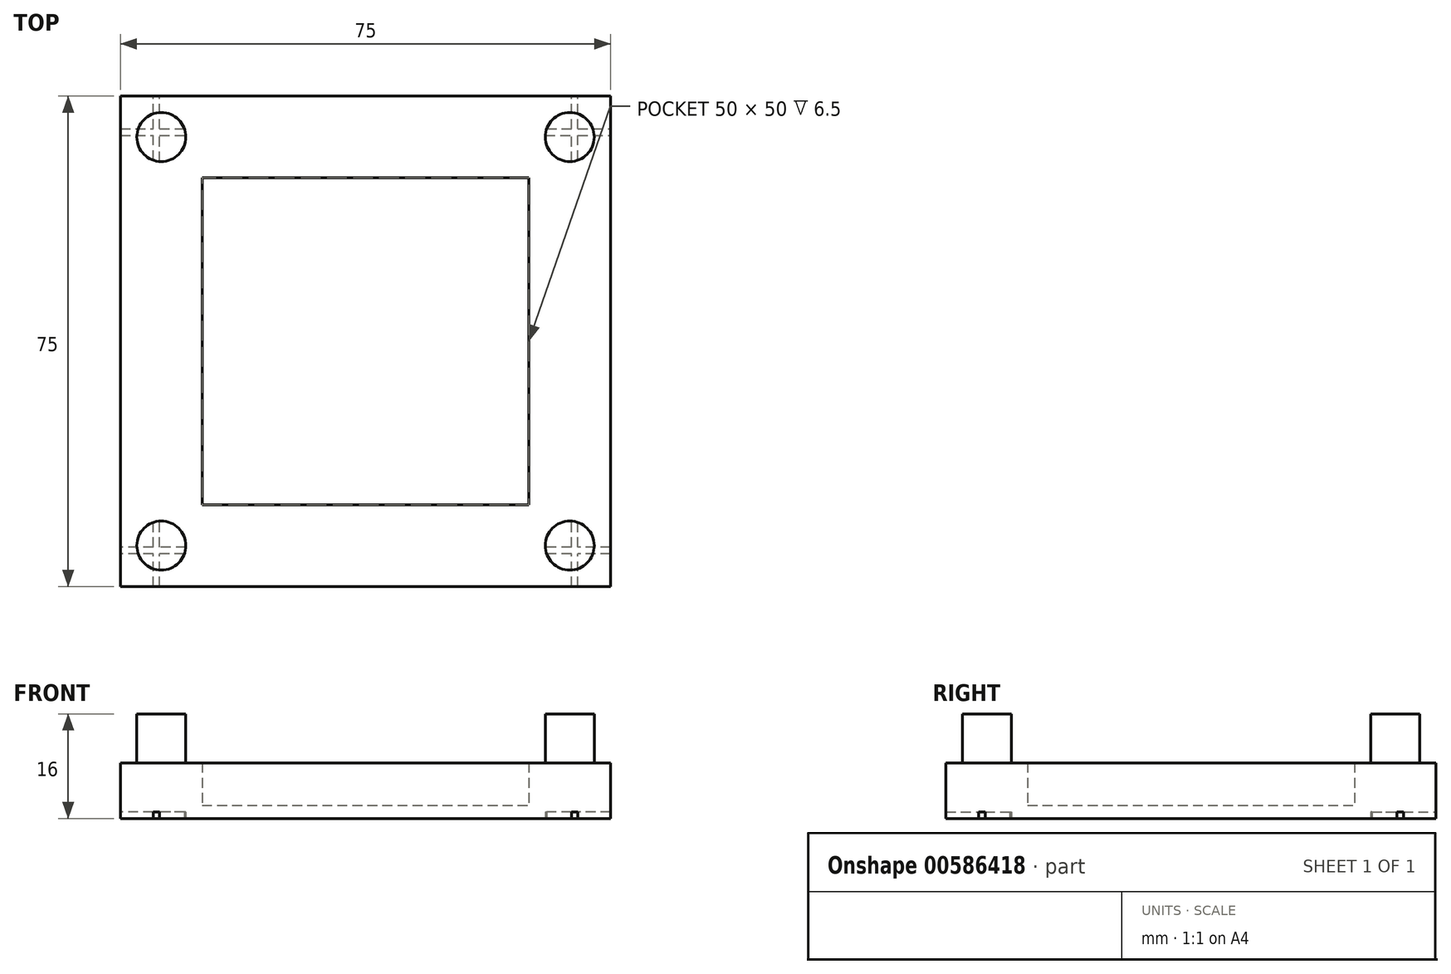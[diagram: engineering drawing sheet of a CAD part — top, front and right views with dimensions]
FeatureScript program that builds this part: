
annotation { "Feature Type Name" : "Feature", "Feature Type Description" : "" }
export const myFeature = defineFeature(function(context is Context, id is Id, definition is map)
    precondition{}
    {
        {
            var Q0;
            Q0=qCreatedBy(makeId("Top.planeOp"),FACE);
            var sketch = newSketch(context, id + "F0", { "sketchPlane" : qUnion([Q0])});
            skLineSegment(sketch, "E0.bottom", {"start": v(-37.5, -37.5) * mm, "end": v(37.5, -37.5) * mm});
            skLineSegment(sketch, "E0.top", {"start": v(-37.5, 37.5) * mm, "end": v(37.5, 37.5) * mm});
            skLineSegment(sketch, "E0.left", {"start": v(-37.5, -37.5) * mm, "end": v(-37.5, 37.5) * mm});
            skLineSegment(sketch, "E0.right", {"start": v(37.5, -37.5) * mm, "end": v(37.5, 37.5) * mm});
            skPoint(sketch, "E0.middle", {"position": v(0, 0) * mm});
            skCircle(sketch, "E1", {"center": v(-31.25, 31.25) * mm, "radius": 3.75 * mm});
            skCircle(sketch, "E2", {"center": v(31.25, 31.25) * mm, "radius": 3.75 * mm});
            skCircle(sketch, "E3", {"center": v(31.25, -31.25) * mm, "radius": 3.75 * mm});
            skCircle(sketch, "E4", {"center": v(-31.25, -31.25) * mm, "radius": 3.75 * mm});
            skSolve(sketch);
        }
        {
            var Q0;
            Q0=makeQuery(id+"F0.imprint","IMPRINT",FACE,{"disambiguationData":[TD([[makeQuery(id+"F0.imprint","IMPRINT",EDGE,{"derivedFrom":sQuery(id+"F0.wireOp",EDGE,"E0.bottom")}),1.0]])]});
            var Q1;
            Q1=makeQuery(id+"F0.imprint","IMPRINT",FACE,{"disambiguationData":[TD([[makeQuery(id+"F0.imprint","IMPRINT",EDGE,{"derivedFrom":sQuery(id+"F0.wireOp",EDGE,"E1")}),1.0]])]});
            var Q2;
            Q2=makeQuery(id+"F0.imprint","IMPRINT",FACE,{"disambiguationData":[TD([[makeQuery(id+"F0.imprint","IMPRINT",EDGE,{"derivedFrom":sQuery(id+"F0.wireOp",EDGE,"E2")}),1.0]])]});
            var Q3;
            Q3=makeQuery(id+"F0.imprint","IMPRINT",FACE,{"disambiguationData":[TD([[makeQuery(id+"F0.imprint","IMPRINT",EDGE,{"derivedFrom":sQuery(id+"F0.wireOp",EDGE,"E3")}),1.0]])]});
            var Q4;
            Q4=makeQuery(id+"F0.imprint","IMPRINT",FACE,{"disambiguationData":[TD([[makeQuery(id+"F0.imprint","IMPRINT",EDGE,{"derivedFrom":sQuery(id+"F0.wireOp",EDGE,"E4")}),1.0]])]});
            extrude(context, id + "F1", {"entities" : qUnion([Q0, Q1, Q2, Q3, Q4]), "depth" : 2 * mm, "offsetDistance" : 25 * mm});
        }
        {
            var Q0;
            Q0=makeQuery(id+"F0.imprint","IMPRINT",FACE,{"disambiguationData":[TD([[makeQuery(id+"F0.imprint","IMPRINT",EDGE,{"derivedFrom":sQuery(id+"F0.wireOp",EDGE,"E4")}),1.0]])]});
            var Q1;
            Q1=makeQuery(id+"F0.imprint","IMPRINT",FACE,{"disambiguationData":[TD([[makeQuery(id+"F0.imprint","IMPRINT",EDGE,{"derivedFrom":sQuery(id+"F0.wireOp",EDGE,"E3")}),1.0]])]});
            var Q2;
            Q2=makeQuery(id+"F0.imprint","IMPRINT",FACE,{"disambiguationData":[TD([[makeQuery(id+"F0.imprint","IMPRINT",EDGE,{"derivedFrom":sQuery(id+"F0.wireOp",EDGE,"E1")}),1.0]])]});
            var Q3;
            Q3=makeQuery(id+"F0.imprint","IMPRINT",FACE,{"disambiguationData":[TD([[makeQuery(id+"F0.imprint","IMPRINT",EDGE,{"derivedFrom":sQuery(id+"F0.wireOp",EDGE,"E2")}),1.0]])]});
            extrude(context, id + "F2", {"entities" : qUnion([Q0, Q1, Q2, Q3]), "operationType" : NewBodyOperationType.ADD, "depth" : 16 * mm, "offsetDistance" : 25 * mm});
        }
        {
            var Q0;
            Q0=makeQuery(id+"F1.opExtrude","CAP_FACE",FACE,{"disambiguationData":[OSD([sQuery(id+"F0.wireOp",EDGE,"E0.bottom"),sQuery(id+"F0.wireOp",EDGE,"E0.top"),sQuery(id+"F0.wireOp",EDGE,"E0.left"),sQuery(id+"F0.wireOp",EDGE,"E0.right")])],"isStart":false});
            var sketch = newSketch(context, id + "F3", { "sketchPlane" : qUnion([Q0])});
            skLineSegment(sketch, "E5.bottom", {"start": v(-25, -25) * mm, "end": v(25, -25) * mm});
            skLineSegment(sketch, "E5.top", {"start": v(-25, 25) * mm, "end": v(25, 25) * mm});
            skLineSegment(sketch, "E5.left", {"start": v(-25, -25) * mm, "end": v(-25, 25) * mm});
            skLineSegment(sketch, "E5.right", {"start": v(25, -25) * mm, "end": v(25, 25) * mm});
            skPoint(sketch, "E5.middle", {"position": v(0, 0) * mm});
            skSolve(sketch);
        }
        {
            var Q0;
            Q0=makeQuery(id+"F3.imprint","IMPRINT",FACE,{"disambiguationData":[TD([[makeQuery(id+"F3.imprint","IMPRINT",EDGE,{"derivedFrom":sQuery(id+"F3.wireOp",EDGE,"E5.bottom")}),-1.0]])]});
            extrude(context, id + "F4", {"entities" : qUnion([Q0]), "operationType" : NewBodyOperationType.ADD, "depth" : 6.5 * mm, "offsetDistance" : 25 * mm});
        }
        {
            var Q0;
            Q0=makeQuery(id+"F0.imprint","IMPRINT",FACE,{"disambiguationData":[TD([[makeQuery(id+"F0.imprint","IMPRINT",EDGE,{"derivedFrom":sQuery(id+"F0.wireOp",EDGE,"E0.bottom")}),1.0]])]});
            var sketch = newSketch(context, id + "F5", { "sketchPlane" : qUnion([Q0])});
            skLineSegment(sketch, "E6.bottom", {"start": v(-32.5, -37.5) * mm, "end": v(-31.5, -37.5) * mm});
            skLineSegment(sketch, "E6.top", {"start": v(-32.5, 37.5) * mm, "end": v(-31.5, 37.5) * mm});
            skLineSegment(sketch, "E6.left", {"start": v(-32.5, -37.5) * mm, "end": v(-32.5, 37.5) * mm});
            skLineSegment(sketch, "E6.right", {"start": v(-31.5, -37.5) * mm, "end": v(-31.5, 37.5) * mm});
            skLineSegment(sketch, "E7.bottom", {"start": v(31.5, -37.5) * mm, "end": v(32.5, -37.5) * mm});
            skLineSegment(sketch, "E7.top", {"start": v(31.5, 37.5) * mm, "end": v(32.5, 37.5) * mm});
            skLineSegment(sketch, "E7.left", {"start": v(31.5, -37.5) * mm, "end": v(31.5, 37.5) * mm});
            skLineSegment(sketch, "E7.right", {"start": v(32.5, -37.5) * mm, "end": v(32.5, 37.5) * mm});
            skLineSegment(sketch, "E8.bottom", {"start": v(37.5, -31.5) * mm, "end": v(-37.5, -31.5) * mm});
            skLineSegment(sketch, "E8.top", {"start": v(37.5, -32.5) * mm, "end": v(-37.5, -32.5) * mm});
            skLineSegment(sketch, "E8.left", {"start": v(37.5, -32.5) * mm, "end": v(37.5, -31.5) * mm});
            skLineSegment(sketch, "E8.right", {"start": v(-37.5, -32.5) * mm, "end": v(-37.5, -31.5) * mm});
            skLineSegment(sketch, "E9.bottom", {"start": v(-37.5, 31.5) * mm, "end": v(37.5, 31.5) * mm});
            skLineSegment(sketch, "E9.top", {"start": v(-37.5, 32.5) * mm, "end": v(37.5, 32.5) * mm});
            skLineSegment(sketch, "E9.left", {"start": v(-37.5, 31.5) * mm, "end": v(-37.5, 32.5) * mm});
            skLineSegment(sketch, "E9.right", {"start": v(37.5, 31.5) * mm, "end": v(37.5, 32.5) * mm});
            skSolve(sketch);
        }
        {
            var Q0;
            {var subQ0=sQuery(id+"F5.wireOp",EDGE,"E7.bottom");Q0=makeQuery(id+"F5.imprint","IMPRINT",FACE,{"disambiguationData":[TD([[makeQuery(id+"F5.imprint","IMPRINT",EDGE,{"derivedFrom":subQ0}),1.0]])]});}
            var Q1;
            {var subQ0=sQuery(id+"F5.wireOp",EDGE,"E8.top");var subQ1=sQuery(id+"F5.wireOp",EDGE,"E7.left");var subQ2=makeQuery(id+"F5.imprint","INTERSECT",VERTEX,{"derivedFrom":[subQ1,subQ0]});Q1=makeQuery(id+"F5.imprint","IMPRINT",FACE,{"disambiguationData":[TD([[makeQuery(id+"F5.imprint","IMPRINT",EDGE,{"disambiguationData":[TD([[subQ2,1.0]])],"derivedFrom":subQ1}),-1.0]])]});}
            var Q2;
            {var subQ0=sQuery(id+"F5.wireOp",EDGE,"E8.top");var subQ1=sQuery(id+"F5.wireOp",EDGE,"E7.right");var subQ2=makeQuery(id+"F5.imprint","INTERSECT",VERTEX,{"derivedFrom":[subQ1,subQ0]});Q2=makeQuery(id+"F5.imprint","IMPRINT",FACE,{"disambiguationData":[TD([[makeQuery(id+"F5.imprint","IMPRINT",EDGE,{"disambiguationData":[TD([[subQ2,-1.0]])],"derivedFrom":subQ1}),-1.0]])]});}
            var Q3;
            {var subQ0=sQuery(id+"F5.wireOp",EDGE,"E8.left");Q3=makeQuery(id+"F5.imprint","IMPRINT",FACE,{"disambiguationData":[TD([[makeQuery(id+"F5.imprint","IMPRINT",EDGE,{"derivedFrom":subQ0}),1.0]])]});}
            var Q4;
            {var subQ0=sQuery(id+"F5.wireOp",EDGE,"E8.top");var subQ1=sQuery(id+"F5.wireOp",EDGE,"E7.left");var subQ2=makeQuery(id+"F5.imprint","INTERSECT",VERTEX,{"derivedFrom":[subQ1,subQ0]});Q4=makeQuery(id+"F5.imprint","IMPRINT",FACE,{"disambiguationData":[TD([[makeQuery(id+"F5.imprint","IMPRINT",EDGE,{"disambiguationData":[TD([[subQ2,-1.0]])],"derivedFrom":subQ1}),-1.0]])]});}
            var Q5;
            {var subQ0=sQuery(id+"F5.wireOp",EDGE,"E8.top");var subQ1=sQuery(id+"F5.wireOp",EDGE,"E7.left");var subQ2=makeQuery(id+"F5.imprint","INTERSECT",VERTEX,{"derivedFrom":[subQ1,subQ0]});Q5=makeQuery(id+"F5.imprint","IMPRINT",FACE,{"disambiguationData":[TD([[makeQuery(id+"F5.imprint","IMPRINT",EDGE,{"disambiguationData":[TD([[subQ2,-1.0]])],"derivedFrom":subQ1}),1.0]])]});}
            var Q6;
            {var subQ0=sQuery(id+"F5.wireOp",EDGE,"E8.bottom");var subQ1=sQuery(id+"F5.wireOp",EDGE,"E7.left");var subQ2=makeQuery(id+"F5.imprint","INTERSECT",VERTEX,{"derivedFrom":[subQ1,subQ0]});Q6=makeQuery(id+"F5.imprint","IMPRINT",FACE,{"disambiguationData":[TD([[makeQuery(id+"F5.imprint","IMPRINT",EDGE,{"disambiguationData":[TD([[subQ2,-1.0]])],"derivedFrom":subQ1}),-1.0]])]});}
            var Q7;
            {var subQ0=sQuery(id+"F5.wireOp",EDGE,"E7.left");var subQ1=makeQuery(id+"F0.imprint","IMPRINT",EDGE,{"derivedFrom":sQuery(id+"F0.wireOp",EDGE,"E3")});var subQ2=makeQuery(id+"F5.imprint","INTERSECT",VERTEX,{"disambiguationData":[OD(1.0)],"derivedFrom":[subQ1,subQ0]});Q7=makeQuery(id+"F5.imprint","IMPRINT",FACE,{"disambiguationData":[TD([[makeQuery(id+"F5.imprint","IMPRINT",EDGE,{"disambiguationData":[TD([[subQ2,-1.0]])],"derivedFrom":subQ0}),-1.0]])]});}
            var Q8;
            {var subQ0=sQuery(id+"F5.wireOp",EDGE,"E8.bottom");var subQ1=makeQuery(id+"F0.imprint","IMPRINT",EDGE,{"derivedFrom":sQuery(id+"F0.wireOp",EDGE,"E3")});var subQ2=makeQuery(id+"F5.imprint","INTERSECT",VERTEX,{"disambiguationData":[OD(1.0)],"derivedFrom":[subQ1,subQ0]});Q8=makeQuery(id+"F5.imprint","IMPRINT",FACE,{"disambiguationData":[TD([[makeQuery(id+"F5.imprint","IMPRINT",EDGE,{"disambiguationData":[TD([[subQ2,-1.0]])],"derivedFrom":subQ0}),1.0]])]});}
            var Q9;
            {var subQ0=sQuery(id+"F5.wireOp",EDGE,"E8.top");var subQ1=sQuery(id+"F5.wireOp",EDGE,"E6.left");var subQ2=makeQuery(id+"F5.imprint","INTERSECT",VERTEX,{"derivedFrom":[subQ1,subQ0]});Q9=makeQuery(id+"F5.imprint","IMPRINT",FACE,{"disambiguationData":[TD([[makeQuery(id+"F5.imprint","IMPRINT",EDGE,{"disambiguationData":[TD([[subQ2,-1.0]])],"derivedFrom":subQ1}),-1.0]])]});}
            var Q10;
            {var subQ0=sQuery(id+"F5.wireOp",EDGE,"E8.top");var subQ1=sQuery(id+"F5.wireOp",EDGE,"E6.left");var subQ2=makeQuery(id+"F5.imprint","INTERSECT",VERTEX,{"derivedFrom":[subQ1,subQ0]});Q10=makeQuery(id+"F5.imprint","IMPRINT",FACE,{"disambiguationData":[TD([[makeQuery(id+"F5.imprint","IMPRINT",EDGE,{"disambiguationData":[TD([[subQ2,1.0]])],"derivedFrom":subQ1}),-1.0]])]});}
            var Q11;
            {var subQ0=sQuery(id+"F5.wireOp",EDGE,"E8.top");var subQ1=sQuery(id+"F5.wireOp",EDGE,"E6.right");var subQ2=makeQuery(id+"F5.imprint","INTERSECT",VERTEX,{"derivedFrom":[subQ1,subQ0]});Q11=makeQuery(id+"F5.imprint","IMPRINT",FACE,{"disambiguationData":[TD([[makeQuery(id+"F5.imprint","IMPRINT",EDGE,{"disambiguationData":[TD([[subQ2,-1.0]])],"derivedFrom":subQ1}),-1.0]])]});}
            var Q12;
            {var subQ0=sQuery(id+"F5.wireOp",EDGE,"E8.bottom");var subQ1=sQuery(id+"F5.wireOp",EDGE,"E6.left");var subQ2=makeQuery(id+"F5.imprint","INTERSECT",VERTEX,{"derivedFrom":[subQ1,subQ0]});Q12=makeQuery(id+"F5.imprint","IMPRINT",FACE,{"disambiguationData":[TD([[makeQuery(id+"F5.imprint","IMPRINT",EDGE,{"disambiguationData":[TD([[subQ2,-1.0]])],"derivedFrom":subQ1}),-1.0]])]});}
            var Q13;
            {var subQ0=sQuery(id+"F5.wireOp",EDGE,"E8.right");Q13=makeQuery(id+"F5.imprint","IMPRINT",FACE,{"disambiguationData":[TD([[makeQuery(id+"F5.imprint","IMPRINT",EDGE,{"derivedFrom":subQ0}),-1.0]])]});}
            var Q14;
            {var subQ0=sQuery(id+"F5.wireOp",EDGE,"E8.top");var subQ1=sQuery(id+"F5.wireOp",EDGE,"E6.left");var subQ2=makeQuery(id+"F5.imprint","INTERSECT",VERTEX,{"derivedFrom":[subQ1,subQ0]});Q14=makeQuery(id+"F5.imprint","IMPRINT",FACE,{"disambiguationData":[TD([[makeQuery(id+"F5.imprint","IMPRINT",EDGE,{"disambiguationData":[TD([[subQ2,-1.0]])],"derivedFrom":subQ1}),1.0]])]});}
            var Q15;
            {var subQ0=sQuery(id+"F5.wireOp",EDGE,"E6.bottom");Q15=makeQuery(id+"F5.imprint","IMPRINT",FACE,{"disambiguationData":[TD([[makeQuery(id+"F5.imprint","IMPRINT",EDGE,{"derivedFrom":subQ0}),1.0]])]});}
            var Q16;
            {var subQ0=sQuery(id+"F5.wireOp",EDGE,"E6.left");var subQ1=makeQuery(id+"F0.imprint","IMPRINT",EDGE,{"derivedFrom":sQuery(id+"F0.wireOp",EDGE,"E4")});var subQ2=makeQuery(id+"F5.imprint","INTERSECT",VERTEX,{"disambiguationData":[OD(1.0)],"derivedFrom":[subQ1,subQ0]});Q16=makeQuery(id+"F5.imprint","IMPRINT",FACE,{"disambiguationData":[TD([[makeQuery(id+"F5.imprint","IMPRINT",EDGE,{"disambiguationData":[TD([[subQ2,-1.0]])],"derivedFrom":subQ0}),-1.0]])]});}
            var Q17;
            {var subQ0=sQuery(id+"F5.wireOp",EDGE,"E9.left");Q17=makeQuery(id+"F5.imprint","IMPRINT",FACE,{"disambiguationData":[TD([[makeQuery(id+"F5.imprint","IMPRINT",EDGE,{"derivedFrom":subQ0}),-1.0]])]});}
            var Q18;
            {var subQ0=sQuery(id+"F5.wireOp",EDGE,"E9.bottom");var subQ1=sQuery(id+"F5.wireOp",EDGE,"E6.left");var subQ2=makeQuery(id+"F5.imprint","INTERSECT",VERTEX,{"derivedFrom":[subQ1,subQ0]});Q18=makeQuery(id+"F5.imprint","IMPRINT",FACE,{"disambiguationData":[TD([[makeQuery(id+"F5.imprint","IMPRINT",EDGE,{"disambiguationData":[TD([[subQ2,-1.0]])],"derivedFrom":subQ1}),1.0]])]});}
            var Q19;
            {var subQ0=sQuery(id+"F5.wireOp",EDGE,"E9.bottom");var subQ1=sQuery(id+"F5.wireOp",EDGE,"E6.left");var subQ2=makeQuery(id+"F5.imprint","INTERSECT",VERTEX,{"derivedFrom":[subQ1,subQ0]});Q19=makeQuery(id+"F5.imprint","IMPRINT",FACE,{"disambiguationData":[TD([[makeQuery(id+"F5.imprint","IMPRINT",EDGE,{"disambiguationData":[TD([[subQ2,-1.0]])],"derivedFrom":subQ1}),-1.0]])]});}
            var Q20;
            {var subQ0=sQuery(id+"F5.wireOp",EDGE,"E9.bottom");var subQ1=sQuery(id+"F5.wireOp",EDGE,"E6.left");var subQ2=makeQuery(id+"F5.imprint","INTERSECT",VERTEX,{"derivedFrom":[subQ1,subQ0]});Q20=makeQuery(id+"F5.imprint","IMPRINT",FACE,{"disambiguationData":[TD([[makeQuery(id+"F5.imprint","IMPRINT",EDGE,{"disambiguationData":[TD([[subQ2,1.0]])],"derivedFrom":subQ1}),-1.0]])]});}
            var Q21;
            {var subQ0=sQuery(id+"F5.wireOp",EDGE,"E9.bottom");var subQ1=sQuery(id+"F5.wireOp",EDGE,"E6.right");var subQ2=makeQuery(id+"F5.imprint","INTERSECT",VERTEX,{"derivedFrom":[subQ1,subQ0]});Q21=makeQuery(id+"F5.imprint","IMPRINT",FACE,{"disambiguationData":[TD([[makeQuery(id+"F5.imprint","IMPRINT",EDGE,{"disambiguationData":[TD([[subQ2,-1.0]])],"derivedFrom":subQ1}),-1.0]])]});}
            var Q22;
            {var subQ0=sQuery(id+"F5.wireOp",EDGE,"E9.top");var subQ1=sQuery(id+"F5.wireOp",EDGE,"E6.left");var subQ2=makeQuery(id+"F5.imprint","INTERSECT",VERTEX,{"derivedFrom":[subQ1,subQ0]});Q22=makeQuery(id+"F5.imprint","IMPRINT",FACE,{"disambiguationData":[TD([[makeQuery(id+"F5.imprint","IMPRINT",EDGE,{"disambiguationData":[TD([[subQ2,-1.0]])],"derivedFrom":subQ1}),-1.0]])]});}
            var Q23;
            {var subQ0=sQuery(id+"F5.wireOp",EDGE,"E6.top");Q23=makeQuery(id+"F5.imprint","IMPRINT",FACE,{"disambiguationData":[TD([[makeQuery(id+"F5.imprint","IMPRINT",EDGE,{"derivedFrom":subQ0}),-1.0]])]});}
            var Q24;
            {var subQ0=sQuery(id+"F5.wireOp",EDGE,"E9.bottom");var subQ1=makeQuery(id+"F0.imprint","IMPRINT",EDGE,{"derivedFrom":sQuery(id+"F0.wireOp",EDGE,"E1")});var subQ2=makeQuery(id+"F5.imprint","INTERSECT",VERTEX,{"disambiguationData":[OD(1.0)],"derivedFrom":[subQ1,subQ0]});Q24=makeQuery(id+"F5.imprint","IMPRINT",FACE,{"disambiguationData":[TD([[makeQuery(id+"F5.imprint","IMPRINT",EDGE,{"disambiguationData":[TD([[subQ2,-1.0]])],"derivedFrom":subQ0}),1.0]])]});}
            var Q25;
            {var subQ0=sQuery(id+"F5.wireOp",EDGE,"E9.bottom");var subQ1=sQuery(id+"F5.wireOp",EDGE,"E7.left");var subQ2=makeQuery(id+"F5.imprint","INTERSECT",VERTEX,{"derivedFrom":[subQ1,subQ0]});Q25=makeQuery(id+"F5.imprint","IMPRINT",FACE,{"disambiguationData":[TD([[makeQuery(id+"F5.imprint","IMPRINT",EDGE,{"disambiguationData":[TD([[subQ2,-1.0]])],"derivedFrom":subQ1}),1.0]])]});}
            var Q26;
            {var subQ0=sQuery(id+"F5.wireOp",EDGE,"E9.bottom");var subQ1=sQuery(id+"F5.wireOp",EDGE,"E7.left");var subQ2=makeQuery(id+"F5.imprint","INTERSECT",VERTEX,{"derivedFrom":[subQ1,subQ0]});Q26=makeQuery(id+"F5.imprint","IMPRINT",FACE,{"disambiguationData":[TD([[makeQuery(id+"F5.imprint","IMPRINT",EDGE,{"disambiguationData":[TD([[subQ2,1.0]])],"derivedFrom":subQ1}),-1.0]])]});}
            var Q27;
            {var subQ0=sQuery(id+"F5.wireOp",EDGE,"E9.bottom");var subQ1=sQuery(id+"F5.wireOp",EDGE,"E7.right");var subQ2=makeQuery(id+"F5.imprint","INTERSECT",VERTEX,{"derivedFrom":[subQ1,subQ0]});Q27=makeQuery(id+"F5.imprint","IMPRINT",FACE,{"disambiguationData":[TD([[makeQuery(id+"F5.imprint","IMPRINT",EDGE,{"disambiguationData":[TD([[subQ2,-1.0]])],"derivedFrom":subQ1}),-1.0]])]});}
            var Q28;
            {var subQ0=sQuery(id+"F5.wireOp",EDGE,"E9.bottom");var subQ1=sQuery(id+"F5.wireOp",EDGE,"E7.left");var subQ2=makeQuery(id+"F5.imprint","INTERSECT",VERTEX,{"derivedFrom":[subQ1,subQ0]});Q28=makeQuery(id+"F5.imprint","IMPRINT",FACE,{"disambiguationData":[TD([[makeQuery(id+"F5.imprint","IMPRINT",EDGE,{"disambiguationData":[TD([[subQ2,-1.0]])],"derivedFrom":subQ1}),-1.0]])]});}
            var Q29;
            {var subQ0=sQuery(id+"F5.wireOp",EDGE,"E9.top");var subQ1=sQuery(id+"F5.wireOp",EDGE,"E7.left");var subQ2=makeQuery(id+"F5.imprint","INTERSECT",VERTEX,{"derivedFrom":[subQ1,subQ0]});Q29=makeQuery(id+"F5.imprint","IMPRINT",FACE,{"disambiguationData":[TD([[makeQuery(id+"F5.imprint","IMPRINT",EDGE,{"disambiguationData":[TD([[subQ2,-1.0]])],"derivedFrom":subQ1}),-1.0]])]});}
            var Q30;
            {var subQ0=sQuery(id+"F5.wireOp",EDGE,"E7.top");Q30=makeQuery(id+"F5.imprint","IMPRINT",FACE,{"disambiguationData":[TD([[makeQuery(id+"F5.imprint","IMPRINT",EDGE,{"derivedFrom":subQ0}),-1.0]])]});}
            var Q31;
            {var subQ0=sQuery(id+"F5.wireOp",EDGE,"E9.right");Q31=makeQuery(id+"F5.imprint","IMPRINT",FACE,{"disambiguationData":[TD([[makeQuery(id+"F5.imprint","IMPRINT",EDGE,{"derivedFrom":subQ0}),1.0]])]});}
            extrude(context, id + "F6", {"entities" : qUnion([Q0, Q1, Q2, Q3, Q4, Q5, Q6, Q7, Q8, Q9, Q10, Q11, Q12, Q13, Q14, Q15, Q16, Q17, Q18, Q19, Q20, Q21, Q22, Q23, Q24, Q25, Q26, Q27, Q28, Q29, Q30, Q31]), "operationType" : NewBodyOperationType.REMOVE, "depth" : 1 * mm, "offsetDistance" : 25 * mm});
        }
    });
